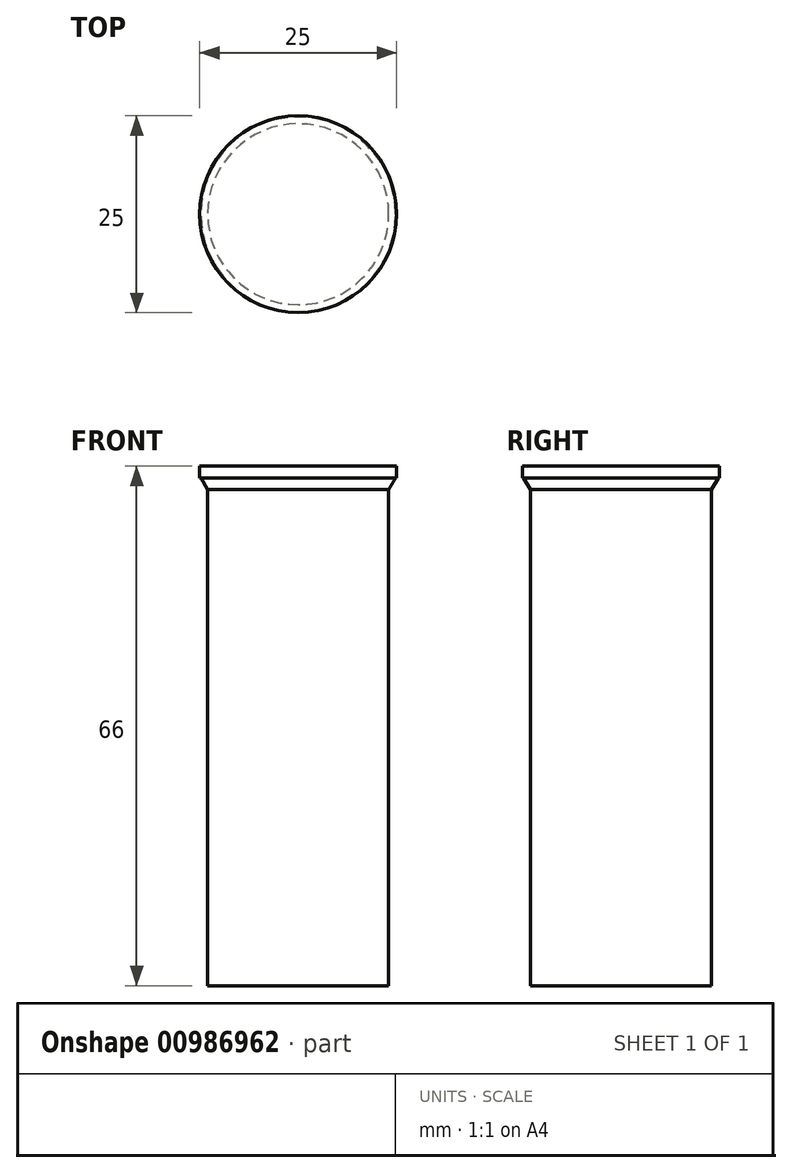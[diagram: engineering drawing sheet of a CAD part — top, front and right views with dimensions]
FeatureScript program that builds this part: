
annotation { "Feature Type Name" : "Feature", "Feature Type Description" : "" }
export const myFeature = defineFeature(function(context is Context, id is Id, definition is map)
    precondition{}
    {
        {
            var Q0;
            Q0=qCreatedBy(makeId("Top.planeOp"),FACE);
            var sketch = newSketch(context, id + "F0", { "sketchPlane" : qUnion([Q0])});
            skCircle(sketch, "E0", {"center": v(0, 0) * mm, "radius": 12.5 * mm});
            skSolve(sketch);
        }
        {
            var Q0;
            Q0 = qSketchRegion(id + "F0", true);
            extrude(context, id + "F1", {"entities" : qUnion([Q0]), "oppositeDirection" : true, "depth" : 1.5 * mm, "offsetDistance" : 25 * mm});
        }
        {
            var Q0;
            Q0=makeQuery(id+"F1.opExtrude","CAP_EDGE",EDGE,{"disambiguationData":[OSD([sQuery(id+"F0.wireOp",EDGE,"E0")])],"isStart":false});
            chamfer(context, id + "F2", {"entities" : qUnion([Q0]), "chamferType" : ChamferType.OFFSET_ANGLE, "width" : 1 * mm, "oppositeDirection" : true, "angle" : 60 * degree, "tangentPropagation" : true});
        }
        {
            var Q0;
            Q0 = qSketchRegion(id + "F0", true);
            extrude(context, id + "F3", {"entities" : qUnion([Q0]), "operationType" : NewBodyOperationType.ADD, "depth" : 1.5 * mm, "offsetDistance" : 25 * mm});
        }
        {
            var Q0;
            Q0=makeQuery(id+"F1.opExtrude","CAP_FACE",FACE,{"disambiguationData":[OSD([sQuery(id+"F0.wireOp",EDGE,"E0")])],"isStart":false});
            extrude(context, id + "F4", {"entities" : qUnion([Q0]), "operationType" : NewBodyOperationType.ADD, "depth" : 63 * mm, "offsetDistance" : 25 * mm});
        }
    });
